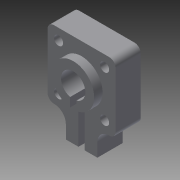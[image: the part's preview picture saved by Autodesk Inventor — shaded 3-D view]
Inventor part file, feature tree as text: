
AUTODESK INVENTOR PART (.ipt)
format: ipt  version: 2014 (Build 180170000, 170)  size: 156,672 bytes
history: native  units: in
note: dims shown in document units (in); Inventor stores cm internally (conversion verified against a paired STEP export)
features: fillet x4, extrude x3, sketch x3
ambient origin geometry x8: Origin, YZ Plane, XZ Plane, XY Plane, X Axis, Y Axis, Z Axis, Center Point
bodies: Solid1 (feature_tree)
feature tree (10):
  extrude  "Extrusion1"  Depth=0.5in
  extrude  "Extrusion2"  Depth=0.81in
  fillet  "Fillet1"  Radius=0.81in
  fillet  "Fillet2"  Radius=0.108in
  fillet  "Fillet3"  [1 undecoded]
  fillet  "Fillet4"  Radius=0.108in
  extrude  "Extrusion3"  Depth=0.4in
  sketch  "Sketch1"  dims[d7=0.2894in d8=0.5in]
  sketch  "Sketch2"  dims[d9=0.81in d11=0.405in d14=0.81in d15=0.108in d16=45.0deg d18=0.108in]
  sketch  "Sketch3"  dims[d19=45.0deg d20=0.548in d21=0.108in d22=0.108in d23=0.548in d25=0.81in d27=0.81in d28=0.405in d34=0.375in d35=0.3in d36=0.0in d37=0.5in d38=0.1in d39=0.0in d40=0.075in d41=0.075in d42=0.075in d43=0.075in d44=0.1875in d45=0.15in d46=0.15in d47=0.4in d48=0.0in]
note: 1 required parameter value undecoded (feature->parameter linkage not recoverable at this tier; creation-order binding heuristic only, values carry confidence <= 0.55)
